FCSTD DOCUMENT  (FreeCAD 0.19R24276 (Git))
Label: Out_gear_t176_w7_d185_GT2_t295_v1
License: All rights reserved
LicenseURL: http://en.wikipedia.org/wiki/All_rights_reserved
objects: App::FeaturePython×4, PartDesign::FeaturePython×1, PartDesign::Body×1, Part::Cylinder×1, Part::Cut×1, Part::FeaturePython×1
note: 5 computed .brp shape members not serialized (recipe doc carries the construction recipe); baked Part::Feature solids carry a one-line shape summary decoded from their .brp

FEATURE [PartDesign::FeaturePython] involutegear001  # WARN: FeaturePython — macro-defined, semantics opaque (R4)
  AttacherType = Attacher::AttachEngine3D
  backlash = 0
  beta = 0
  clearance = 0.25
  da = 178
  df = 173.5
  double_helix = false
  dw = 176
  head = 0
  height = 7
  module = 1
  numpoints = 6
  pressure_angle = 20
  properties_from_tool = false
  reversed_backlash = false
  shift = 0
  simple = false
  teeth = 176
  transverse_pitch = 3.14159
  undercut = false
  version = 0.0.3
FEATURE [PartDesign::Body] Body
  Group = -> [involutegear001]
  Origin = -> Origin
  Tip = -> involutegear001
FEATURE [Part::Cylinder] Cylinder  label="Цилиндр"
  Angle = 360
  AttacherType = Attacher::AttachEngine3D
  Height = 7
  Radius = 92.5
FEATURE [Part::Cut] Cut
  Base = -> Cylinder
  Placement = pos=(-5.56397e-06,-3.36712e-06,-8.34e-13) rot=(0,0,1;0rad)
  Tool = -> Body
FEATURE [Part::FeaturePython] b_GT2_t295_d185_001_  label="GT2_t295_d185_001"  # a2plus imported part (geometry in sourceFile) (typed FeaturePython)
  a2p_Version = V0.1
  fixedPosition = true
  objectType = a2pPart
  sourceFile = .\GT2_t295_d185.FCStd
  subassemblyImport = false
  timeLastImport = 1.6473e+09
  updateColors = true
FEATURE [App::FeaturePython] planeCoincident_001  label="planeCoincident_001__GT2_t295_d185_001"  # a2plus constraint (typed FeaturePython)
  Object1 = Cut
  Object2 = b_GT2_t295_d185_001_
  ParentTreeObject = -> Cut
  SubElement1 = Face2
  SubElement2 = Face5
  Suppressed = false
  Type = plane
  directionConstraint = 0
  offset = 0
FEATURE [App::FeaturePython] planeCoincident_001_mirror  label="planeCoincident_001__Cut"  # a2plus constraint (typed FeaturePython)
  Object1 = Cut
  Object2 = b_GT2_t295_d185_001_
  ParentTreeObject = -> b_GT2_t295_d185_001_
  SubElement1 = Face2
  SubElement2 = Face5
  Suppressed = false
  Type = plane
  directionConstraint = 0
  offset = 0
FEATURE [App::FeaturePython] axisCoincident_001  label="axisCoincident_001__Cut"  # a2plus constraint (typed FeaturePython)
  Object1 = b_GT2_t295_d185_001_
  Object2 = Cut
  ParentTreeObject = -> b_GT2_t295_d185_001_
  SubElement1 = Face1773
  SubElement2 = Face1
  Suppressed = false
  Type = axial
  directionConstraint = 1
  lockRotation = false
FEATURE [App::FeaturePython] axisCoincident_001_mirror  label="axisCoincident_001__GT2_t295_d185_001"  # a2plus constraint (typed FeaturePython)
  Object1 = b_GT2_t295_d185_001_
  Object2 = Cut
  ParentTreeObject = -> Cut
  SubElement1 = Face1773
  SubElement2 = Face1
  Suppressed = false
  Type = axial
  directionConstraint = 1
  lockRotation = false
